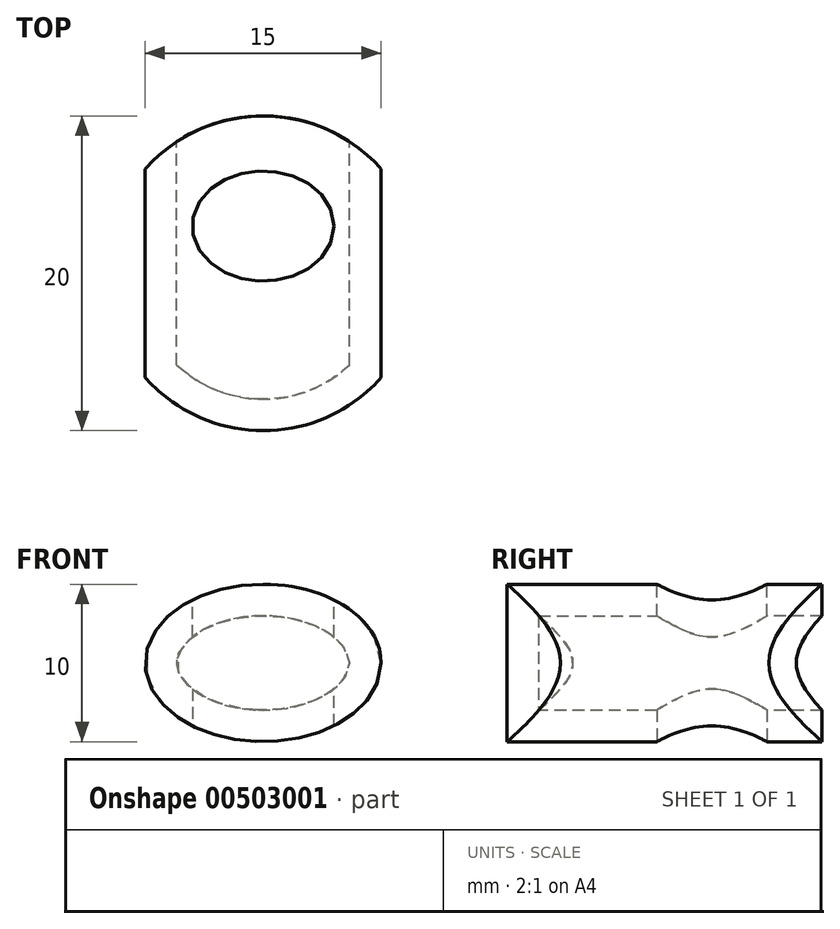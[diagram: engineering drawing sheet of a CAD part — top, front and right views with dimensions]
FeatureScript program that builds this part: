
annotation { "Feature Type Name" : "Feature", "Feature Type Description" : "" }
export const myFeature = defineFeature(function(context is Context, id is Id, definition is map)
    precondition{}
    {
        {
            var Q0;
            Q0=qCreatedBy(makeId("Front.planeOp"),FACE);
            var sketch = newSketch(context, id + "F0", { "sketchPlane" : qUnion([Q0])});
            skEllipse(sketch, "E0", {"center": v(0, 0) * mm, "majorRadius": 7.5 * mm, "minorRadius": 5 * mm, "majorAxis": v(1, 0)});
            skSolve(sketch);
        }
        {
            var Q0;
            Q0 = qSketchRegion(id + "F0", true);
            extrude(context, id + "F1", {"entities" : qUnion([Q0]), "endBound" : BoundingType.SYMMETRIC, "depth" : 20 * mm});
        }
        {
            var Q0;
            Q0=qCreatedBy(makeId("Top.planeOp"),FACE);
            var sketch = newSketch(context, id + "F2", { "sketchPlane" : qUnion([Q0])});
            skCircle(sketch, "E1", {"center": v(0, 0) * mm, "radius": 10 * mm});
            skCircle(sketch, "E2", {"center": v(0, 0) * mm, "radius": 19.17 * mm});
            skSolve(sketch);
        }
        {
            var Q0;
            Q0=makeQuery(id+"F2.imprint","IMPRINT",FACE,{"disambiguationData":[TD([[makeQuery(id+"F2.imprint","IMPRINT",EDGE,{"derivedFrom":sQuery(id+"F2.wireOp",EDGE,"E1")}),-1.0]])]});
            extrude(context, id + "F3", {"entities" : qUnion([Q0]), "operationType" : NewBodyOperationType.REMOVE, "endBound" : BoundingType.SYMMETRIC, "depth" : 25 * mm});
        }
        {
            var Q0;
            Q0=makeQuery(id+"F3.boolean.opBoolean","COPY",FACE,{"disambiguationData":[OD(1.0)],"derivedFrom":makeQuery(id+"F3.opExtrude","SWEPT_FACE",FACE,{"disambiguationData":[OSD([sQuery(id+"F2.wireOp",EDGE,"E1")])]})});
            shell(context, id + "F4", {"entities" : qUnion([Q0]), "thickness" : 2 * mm});
        }
        {
            var Q0;
            Q0=qCreatedBy(makeId("Top.planeOp"),FACE);
            var sketch = newSketch(context, id + "F5", { "sketchPlane" : qUnion([Q0])});
            skEllipse(sketch, "E3", {"center": v(0, 3) * mm, "majorRadius": 4.5 * mm, "minorRadius": 3.5 * mm, "majorAxis": v(1, 0)});
            skSolve(sketch);
        }
        {
            var Q0;
            Q0 = qSketchRegion(id + "F5", true);
            extrude(context, id + "F6", {"entities" : qUnion([Q0]), "operationType" : NewBodyOperationType.REMOVE, "endBound" : BoundingType.SYMMETRIC, "oppositeDirection" : true, "depth" : 25 * mm});
        }
    });
